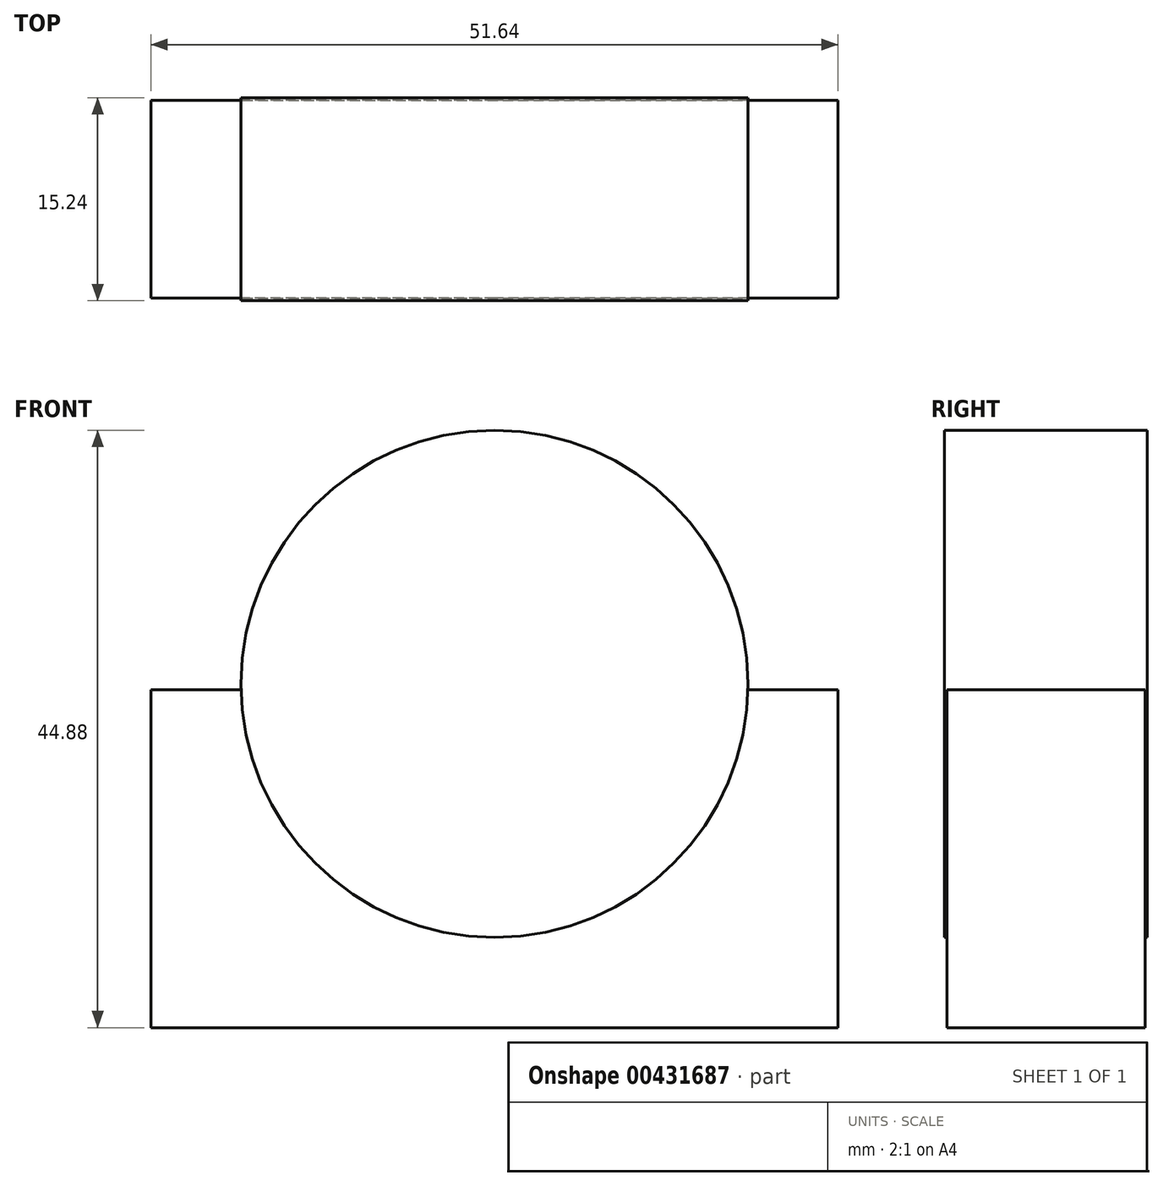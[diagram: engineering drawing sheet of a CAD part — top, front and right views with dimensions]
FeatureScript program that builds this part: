
annotation { "Feature Type Name" : "Feature", "Feature Type Description" : "" }
export const myFeature = defineFeature(function(context is Context, id is Id, definition is map)
    precondition{}
    {
        {
            var Q0;
            Q0=qCreatedBy(makeId("Top.planeOp"),FACE);
            var sketch = newSketch(context, id + "F0", { "sketchPlane" : qUnion([Q0])});
            skLineSegment(sketch, "E0.bottom", {"start": v(-25.82, 7.44) * mm, "end": v(25.82, 7.44) * mm});
            skLineSegment(sketch, "E0.top", {"start": v(-25.82, -7.44) * mm, "end": v(25.82, -7.44) * mm});
            skLineSegment(sketch, "E0.left", {"start": v(-25.82, 7.44) * mm, "end": v(-25.82, -7.44) * mm});
            skLineSegment(sketch, "E0.right", {"start": v(25.82, 7.44) * mm, "end": v(25.82, -7.44) * mm});
            skPoint(sketch, "E0.middle", {"position": v(0, 0) * mm});
            skSolve(sketch);
        }
        {
            var Q0;
            Q0=makeQuery(id+"F0.imprint","IMPRINT",FACE,{"disambiguationData":[TD([[makeQuery(id+"F0.imprint","IMPRINT",EDGE,{"derivedFrom":sQuery(id+"F0.wireOp",EDGE,"E0.bottom")}),-1.0]])]});
            extrude(context, id + "F1", {"entities" : qUnion([Q0]), "depth" : 25.4 * mm});
        }
        {
            var Q0;
            Q0=qCreatedBy(makeId("Front.planeOp"),FACE);
            var sketch = newSketch(context, id + "F2", { "sketchPlane" : qUnion([Q0])});
            skCircle(sketch, "E1", {"center": v(0, 25.83) * mm, "radius": 19.05 * mm});
            skSolve(sketch);
        }
        {
            var Q0;
            Q0=makeQuery(id+"F2.imprint","IMPRINT",FACE,{"disambiguationData":[TD([[makeQuery(id+"F2.imprint","IMPRINT",EDGE,{"derivedFrom":sQuery(id+"F2.wireOp",EDGE,"E1")}),1.0]])]});
            extrude(context, id + "F3", {"entities" : qUnion([Q0]), "operationType" : NewBodyOperationType.ADD, "depth" : 7.62 * mm, "hasSecondDirection" : true, "secondDirectionOppositeDirection" : true, "secondDirectionDepth" : 7.62 * mm});
        }
    });
